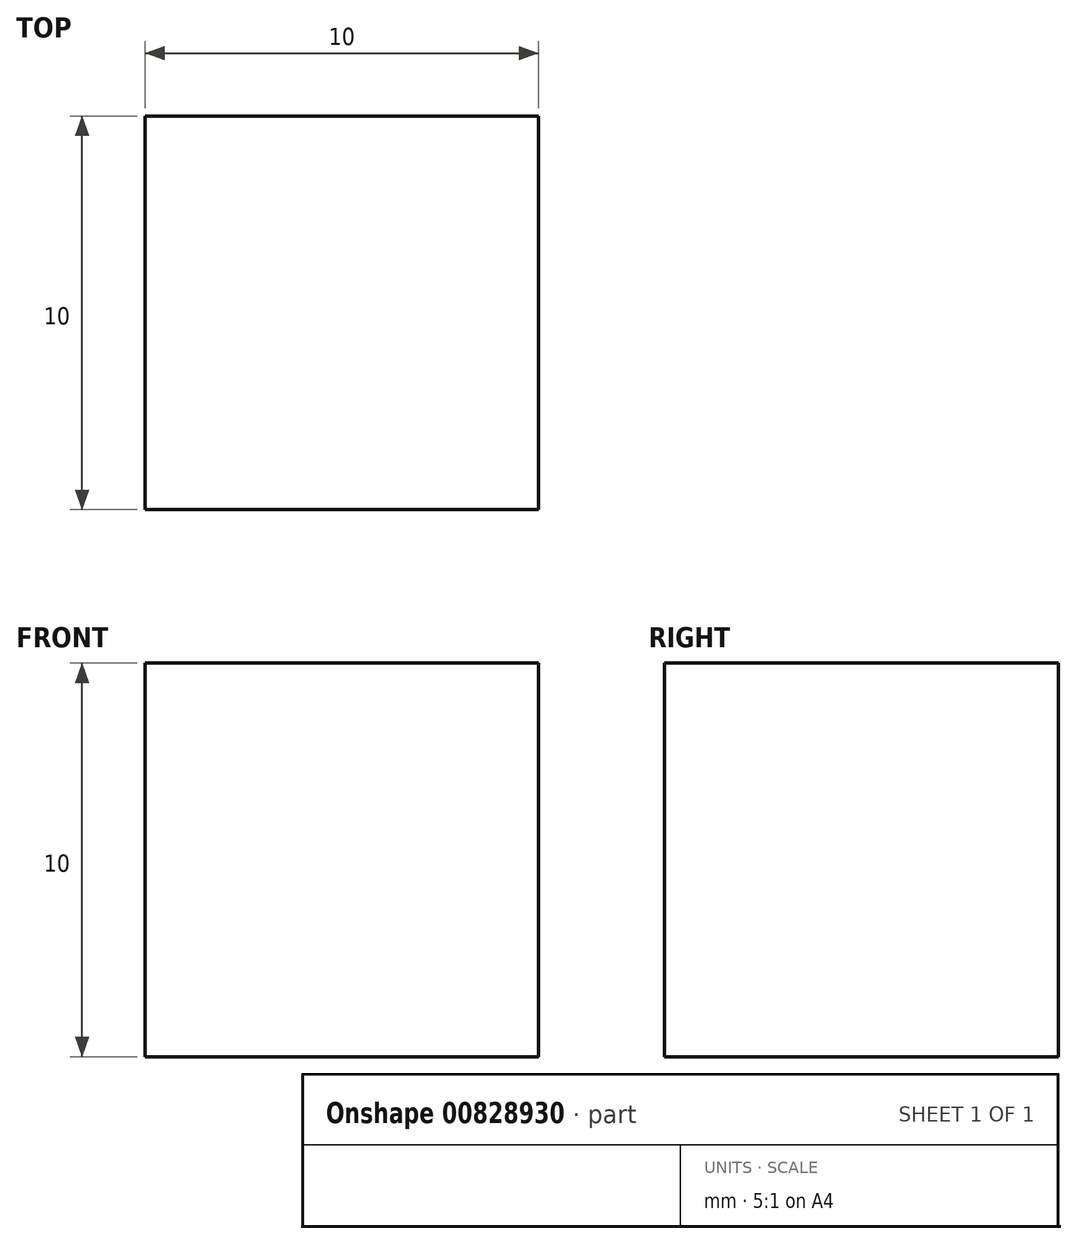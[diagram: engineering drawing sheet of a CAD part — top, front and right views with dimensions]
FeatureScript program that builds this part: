
annotation { "Feature Type Name" : "Feature", "Feature Type Description" : "" }
export const myFeature = defineFeature(function(context is Context, id is Id, definition is map)
    precondition{}
    {
        {
            var Q0;
            Q0=qCreatedBy(makeId("Front.planeOp"),FACE);
            var sketch = newSketch(context, id + "F0", { "sketchPlane" : qUnion([Q0])});
            skLineSegment(sketch, "E0.bottom", {"start": v(5, -5) * mm, "end": v(-5, -5) * mm});
            skLineSegment(sketch, "E0.top", {"start": v(5, 5) * mm, "end": v(-5, 5) * mm});
            skLineSegment(sketch, "E0.left", {"start": v(5, -5) * mm, "end": v(5, 5) * mm});
            skLineSegment(sketch, "E0.right", {"start": v(-5, -5) * mm, "end": v(-5, 5) * mm});
            skPoint(sketch, "E0.middle", {"position": v(0, 0) * mm});
            skSolve(sketch);
        }
        {
            var Q0;
            Q0=qSketchRegion(id+"F0",true);
            extrude(context, id + "F1", {"entities" : qUnion([Q0]), "depth" : 10 * mm, "offsetDistance" : 25 * mm});
        }
    });
